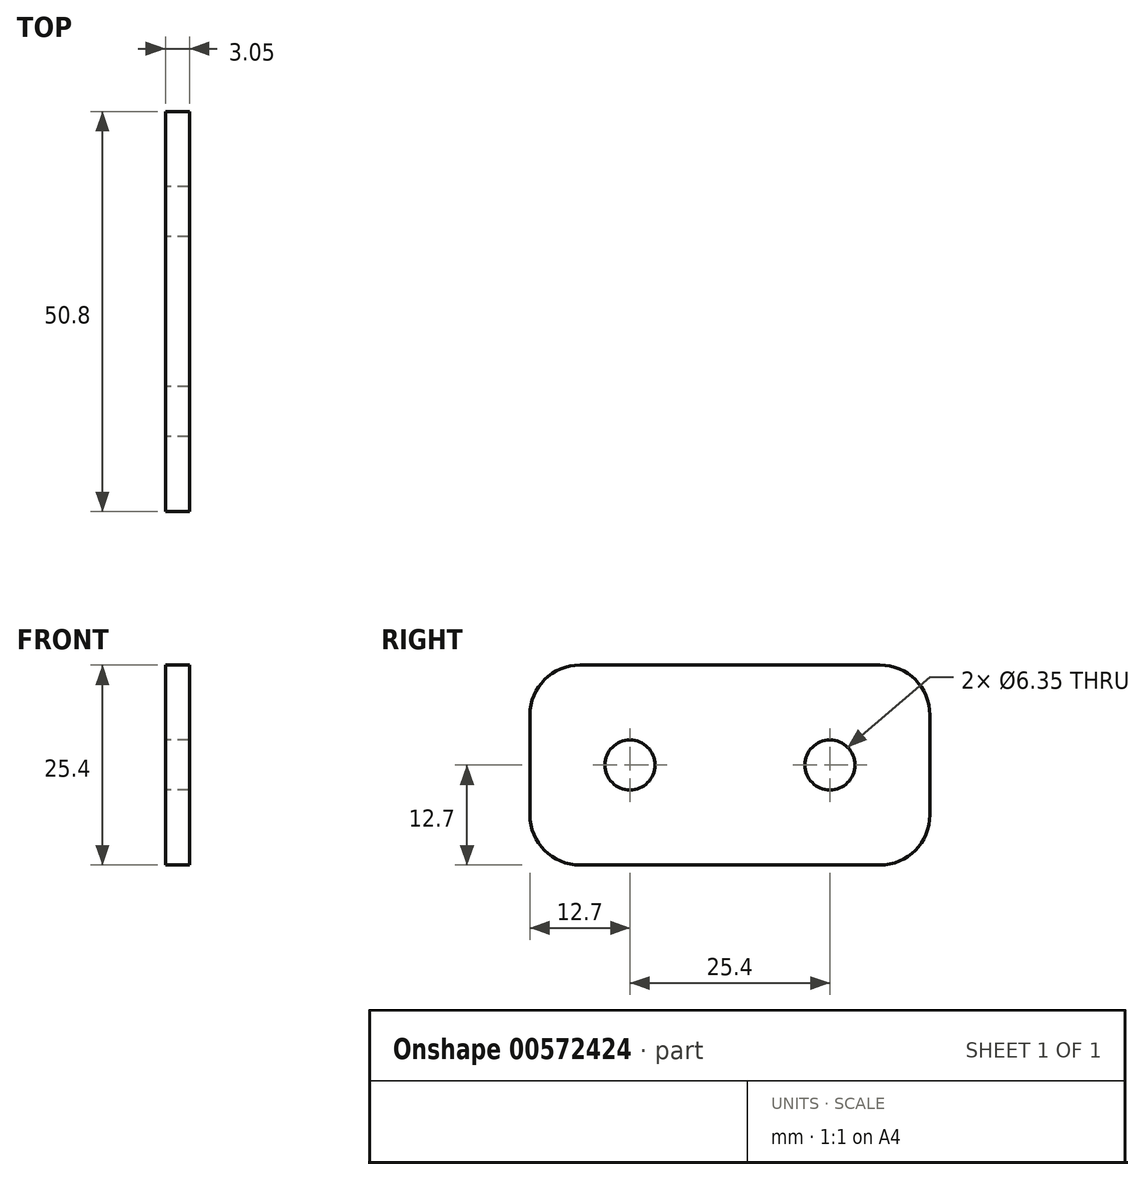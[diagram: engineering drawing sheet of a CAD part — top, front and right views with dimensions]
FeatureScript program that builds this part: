
annotation { "Feature Type Name" : "Feature", "Feature Type Description" : "" }
export const myFeature = defineFeature(function(context is Context, id is Id, definition is map)
    precondition{}
    {
        {
            var Q0;
            Q0=qCreatedBy(makeId("Right.planeOp"),FACE);
            var sketch = newSketch(context, id + "F0", { "sketchPlane" : qUnion([Q0])});
            skCircle(sketch, "E0", {"center": v(38.1, 0) * mm, "radius": 3.18 * mm});
            skLineSegment(sketch, "E1", {"start": v(38.1, 0) * mm, "end": v(38.1, 12.7) * mm, "construction": true});
            skLineSegment(sketch, "E2", {"start": v(38.1, 0) * mm, "end": v(38.1, -12.7) * mm, "construction": true});
            skLineSegment(sketch, "E3", {"start": v(38.1, 12.7) * mm, "end": v(44.45, 12.7) * mm, "construction": true});
            skLineSegment(sketch, "E4.bottom", {"start": v(50.8, 12.7) * mm, "end": v(6.35, 12.7) * mm});
            skLineSegment(sketch, "E4.top", {"start": v(44.45, -12.7) * mm, "end": v(6.35, -12.7) * mm});
            skLineSegment(sketch, "E4.left", {"start": v(50.8, 6.35) * mm, "end": v(50.8, -6.35) * mm});
            skLineSegment(sketch, "E4.right", {"start": v(0, 6.35) * mm, "end": v(0, -6.35) * mm});
            skLineSegment(sketch, "E5", {"start": v(0, 0) * mm, "end": v(12.7, 0) * mm, "construction": true});
            skCircle(sketch, "E6", {"center": v(12.7, 0) * mm, "radius": 3.18 * mm});
            skPoint(sketch, "E7.visualSharp", {"position": v(50.8, 12.7) * mm});
            skArc(sketch, "E7.filletArc", {"start": v(50.8, 6.35) * mm, "mid": v(48.94, 10.84) * mm, "end": v(44.45, 12.7) * mm});
            skPoint(sketch, "E8.visualSharp", {"position": v(50.8, -12.7) * mm});
            skArc(sketch, "E8.filletArc", {"start": v(44.45, -12.7) * mm, "mid": v(48.94, -10.84) * mm, "end": v(50.8, -6.35) * mm});
            skPoint(sketch, "E9.visualSharp", {"position": v(0, 12.7) * mm});
            skArc(sketch, "E9.filletArc", {"start": v(6.35, 12.7) * mm, "mid": v(1.86, 10.84) * mm, "end": v(0, 6.35) * mm});
            skPoint(sketch, "E10.visualSharp", {"position": v(0, -12.7) * mm});
            skArc(sketch, "E10.filletArc", {"start": v(0, -6.35) * mm, "mid": v(1.86, -10.84) * mm, "end": v(6.35, -12.7) * mm});
            skSolve(sketch);
        }
        {
            var Q0;
            Q0=makeQuery(id+"F0.imprint","IMPRINT",FACE,{"disambiguationData":[TD([[makeQuery(id+"F0.imprint","IMPRINT",EDGE,{"derivedFrom":sQuery(id+"F0.wireOp",EDGE,"E0")}),-1.0]])]});
            extrude(context, id + "F1", {"entities" : qUnion([Q0]), "depth" : 3.05 * mm, "offsetDistance" : 25.4 * mm});
        }
    });
